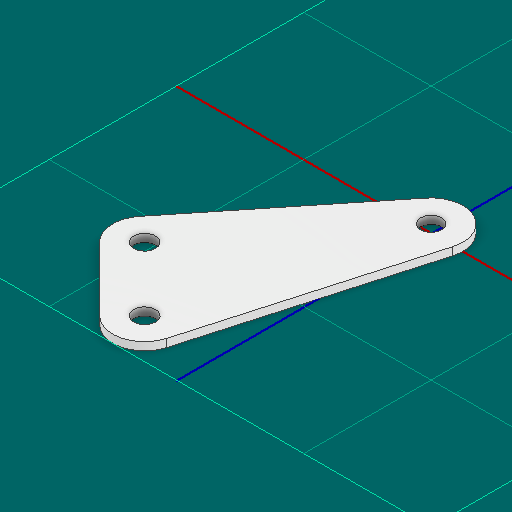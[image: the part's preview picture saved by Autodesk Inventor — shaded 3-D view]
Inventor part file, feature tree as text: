
AUTODESK INVENTOR PART (.ipt)
format: ipt  version: 2025 (Build 290162000, 162)  size: 112,640 bytes
history: native  units: in
note: dims shown in document units (in); Inventor stores cm internally (conversion verified against a paired STEP export)
features: other x5, sketch x1
ambient origin geometry x8: Origin, YZ Plane, XZ Plane, XY Plane, X Axis, Y Axis, Z Axis, Center Point
bodies: Solid1 (feature_tree)
feature tree (6):
  other  "gusset.ipt"
  other  "Blocks"
  other  "main"
  other  "Solid1::gusset.ipt"
  other  "TaggingFeature1"
  sketch  "Sketch1"  dims[d0=0.3937in d1=0.5in]
